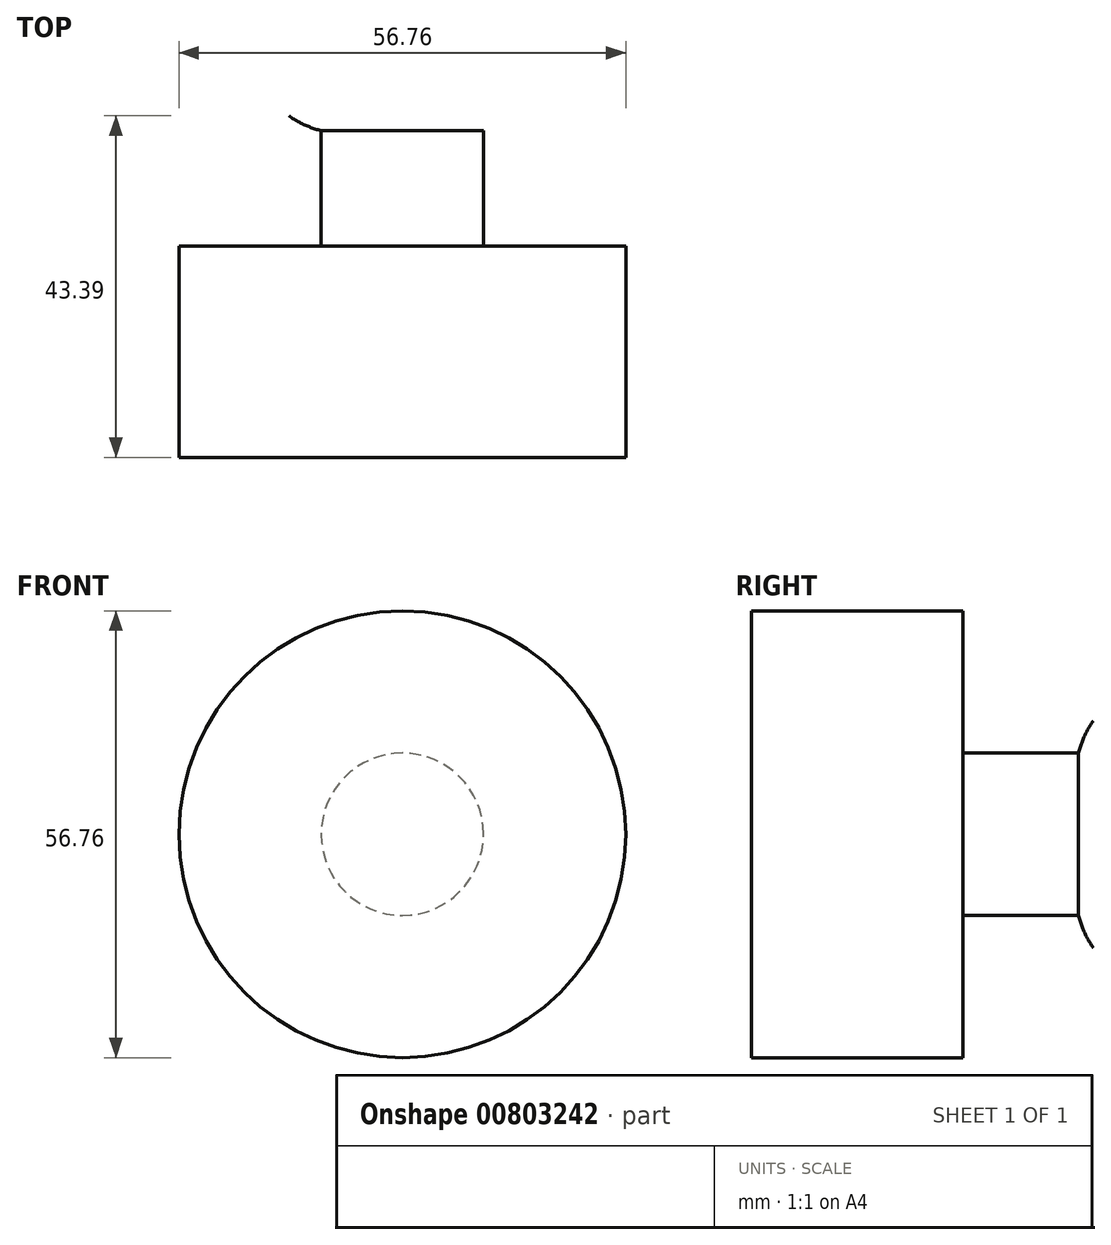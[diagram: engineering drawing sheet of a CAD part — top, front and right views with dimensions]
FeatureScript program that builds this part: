
annotation { "Feature Type Name" : "Feature", "Feature Type Description" : "" }
export const myFeature = defineFeature(function(context is Context, id is Id, definition is map)
    precondition{}
    {
        {
            var Q0;
            Q0=qCreatedBy(makeId("Top.planeOp"),FACE);
            var sketch = newSketch(context, id + "F0", { "sketchPlane" : qUnion([Q0])});
            skLineSegment(sketch, "E0", {"start": v(0, 75) * mm, "end": v(0, -74.64) * mm, "construction": true});
            skLineSegment(sketch, "E1.bottom", {"start": v(10.31, -22.81) * mm, "end": v(28.38, -22.81) * mm});
            skLineSegment(sketch, "E1.top", {"start": v(0, -49.64) * mm, "end": v(28.38, -49.64) * mm});
            skLineSegment(sketch, "E1.left", {"start": v(0, -22.81) * mm, "end": v(0, -49.64) * mm});
            skLineSegment(sketch, "E1.right", {"start": v(28.38, -22.81) * mm, "end": v(28.38, -49.64) * mm});
            skLineSegment(sketch, "E2.left", {"start": v(10.31, -8.14) * mm, "end": v(10.31, -22.81) * mm});
            skLineSegment(sketch, "E2.right", {"start": v(0, 0) * mm, "end": v(0, -28.65) * mm});
            skArc(sketch, "E3", {"start": v(10.31, -8.14) * mm, "mid": v(18.6, 9.26) * mm, "end": v(0, 14.28) * mm});
            skPoint(sketch, "E4.orphan", {"position": v(10.31, 0) * mm});
            skLineSegment(sketch, "E5", {"start": v(0, 14.28) * mm, "end": v(0, -49.64) * mm});
            skSolve(sketch);
        }
        {
            var Q0;
            Q0=makeQuery(id+"F0.imprint","IMPRINT",FACE,{"disambiguationData":[TD([[makeQuery(id+"F0.imprint","IMPRINT",EDGE,{"derivedFrom":sQuery(id+"F0.wireOp",EDGE,"E1.bottom")}),-1.0]])]});
            var Q1;
            Q1=sQuery(id+"F0.wireOp",EDGE,"E0");
            revolve(context, id + "F1", {"surfaceOperationType" : NewSurfaceOperationType.NEW, "entities" : qUnion([Q0]), "axis" : qUnion([Q1]), "revolveType" : RevolveType.FULL});
        }
    });
